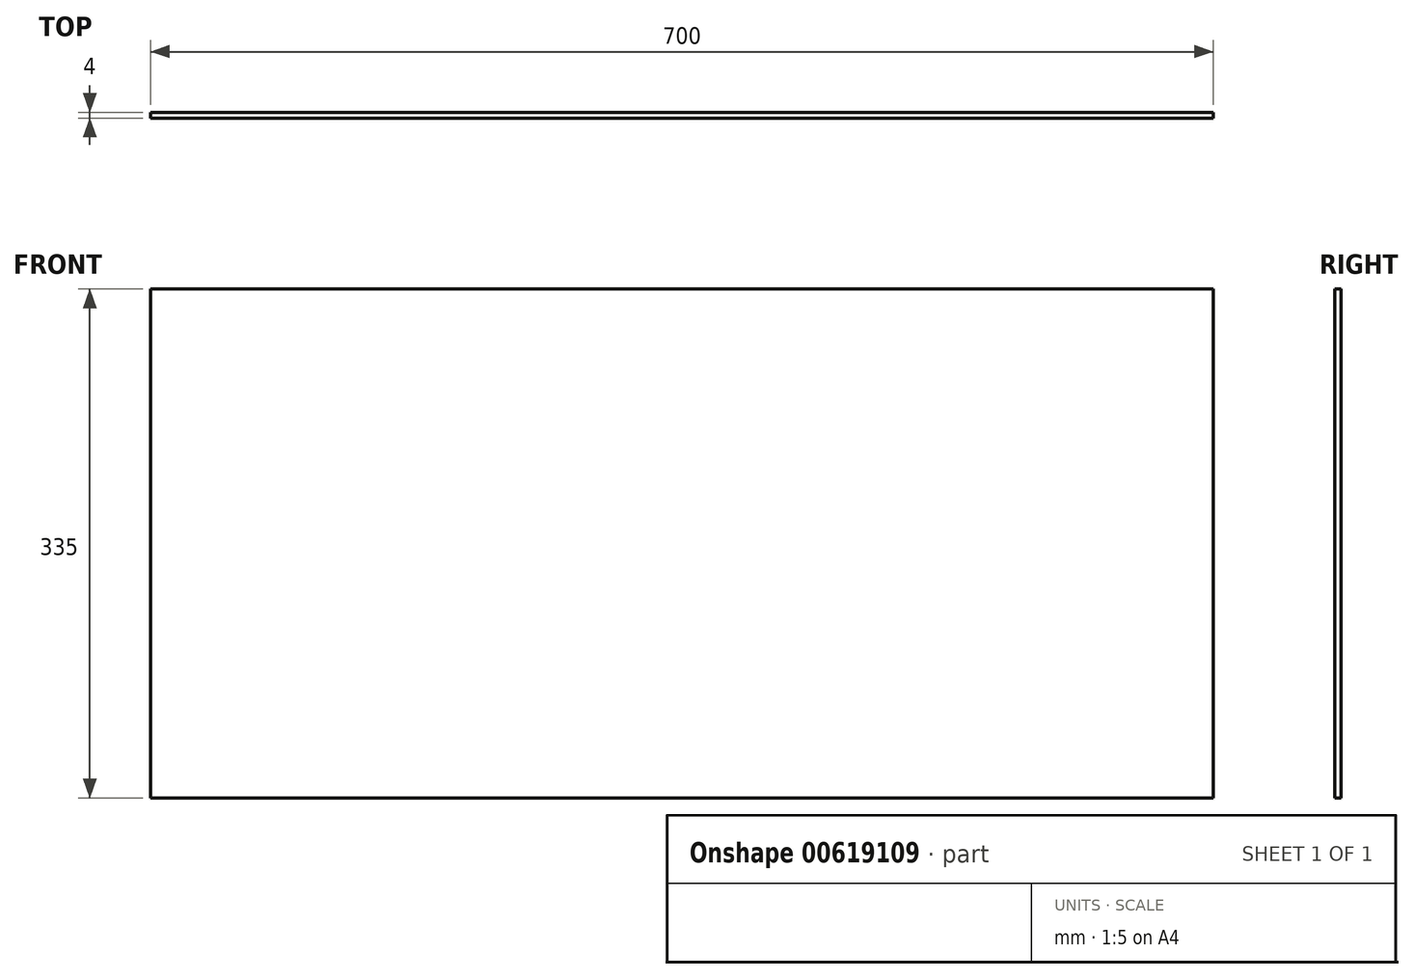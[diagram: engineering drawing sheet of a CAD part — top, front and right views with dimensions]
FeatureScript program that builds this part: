
annotation { "Feature Type Name" : "Feature", "Feature Type Description" : "" }
export const myFeature = defineFeature(function(context is Context, id is Id, definition is map)
    precondition{}
    {
        {
            var Q0;
            Q0=qCreatedBy(makeId("Front.planeOp"),FACE);
            var sketch = newSketch(context, id + "F0", { "sketchPlane" : qUnion([Q0])});
            skLineSegment(sketch, "E0.bottom", {"start": v(350, 167.5) * mm, "end": v(-350, 167.5) * mm});
            skLineSegment(sketch, "E0.top", {"start": v(350, -167.5) * mm, "end": v(-350, -167.5) * mm});
            skLineSegment(sketch, "E0.left", {"start": v(350, 167.5) * mm, "end": v(350, -167.5) * mm});
            skLineSegment(sketch, "E0.right", {"start": v(-350, 167.5) * mm, "end": v(-350, -167.5) * mm});
            skPoint(sketch, "E0.middle", {"position": v(0, 0) * mm});
            skSolve(sketch);
        }
        {
            var Q0;
            Q0=qSketchRegion(id+"F0",true);
            extrude(context, id + "F1", {"entities" : qUnion([Q0]), "depth" : 4 * mm, "offsetDistance" : 25 * mm});
        }
    });
